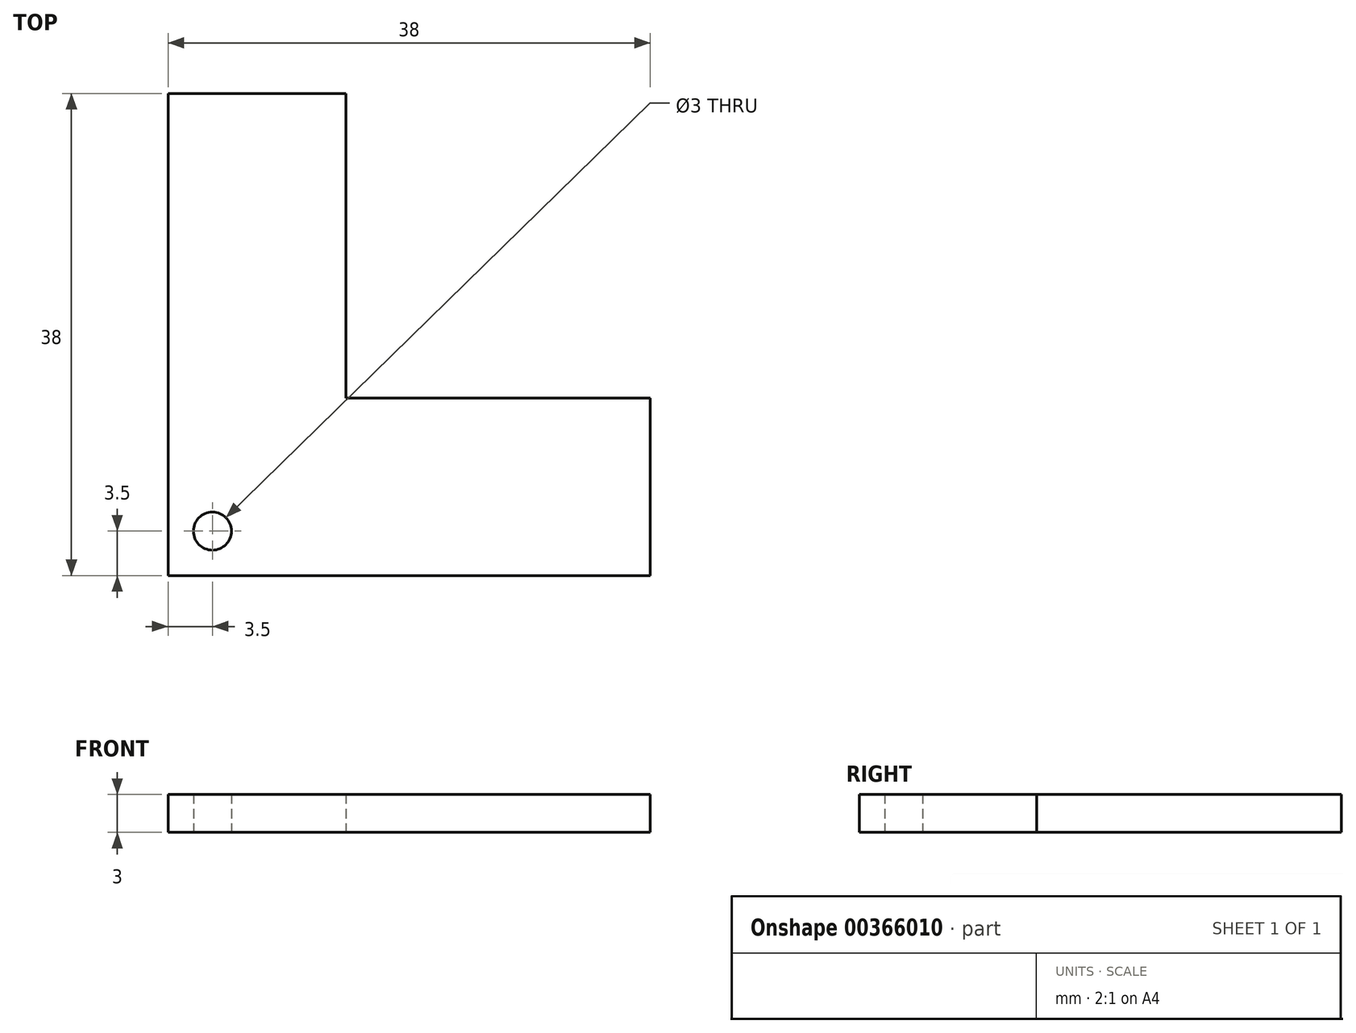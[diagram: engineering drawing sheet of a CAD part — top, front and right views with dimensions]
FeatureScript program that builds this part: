
annotation { "Feature Type Name" : "Feature", "Feature Type Description" : "" }
export const myFeature = defineFeature(function(context is Context, id is Id, definition is map)
    precondition{}
    {
        {
            var Q0;
            Q0=qCreatedBy(makeId("Top.planeOp"),FACE);
            var sketch = newSketch(context, id + "F0", { "sketchPlane" : qUnion([Q0])});
            skLineSegment(sketch, "E0", {"start": v(0, 0) * mm, "end": v(24, 0) * mm});
            skLineSegment(sketch, "E1", {"start": v(24, 0) * mm, "end": v(24, -14) * mm});
            skLineSegment(sketch, "E2", {"start": v(24, -14) * mm, "end": v(-14, -14) * mm});
            skLineSegment(sketch, "E3", {"start": v(-14, -14) * mm, "end": v(-14, 24) * mm});
            skLineSegment(sketch, "E4", {"start": v(-14, 24) * mm, "end": v(0, 24) * mm});
            skLineSegment(sketch, "E5", {"start": v(0, 24) * mm, "end": v(0, 0) * mm});
            skCircle(sketch, "E6", {"center": v(-10.5, -10.5) * mm, "radius": 1.5 * mm});
            skSolve(sketch);
        }
        {
            var Q0;
            Q0=makeQuery(id+"F0.imprint","IMPRINT",FACE,{"disambiguationData":[TD([[makeQuery(id+"F0.imprint","IMPRINT",EDGE,{"derivedFrom":sQuery(id+"F0.wireOp",EDGE,"E0")}),-1.0]])]});
            extrude(context, id + "F1", {"entities" : qUnion([Q0]), "depth" : 3 * mm});
        }
    });
